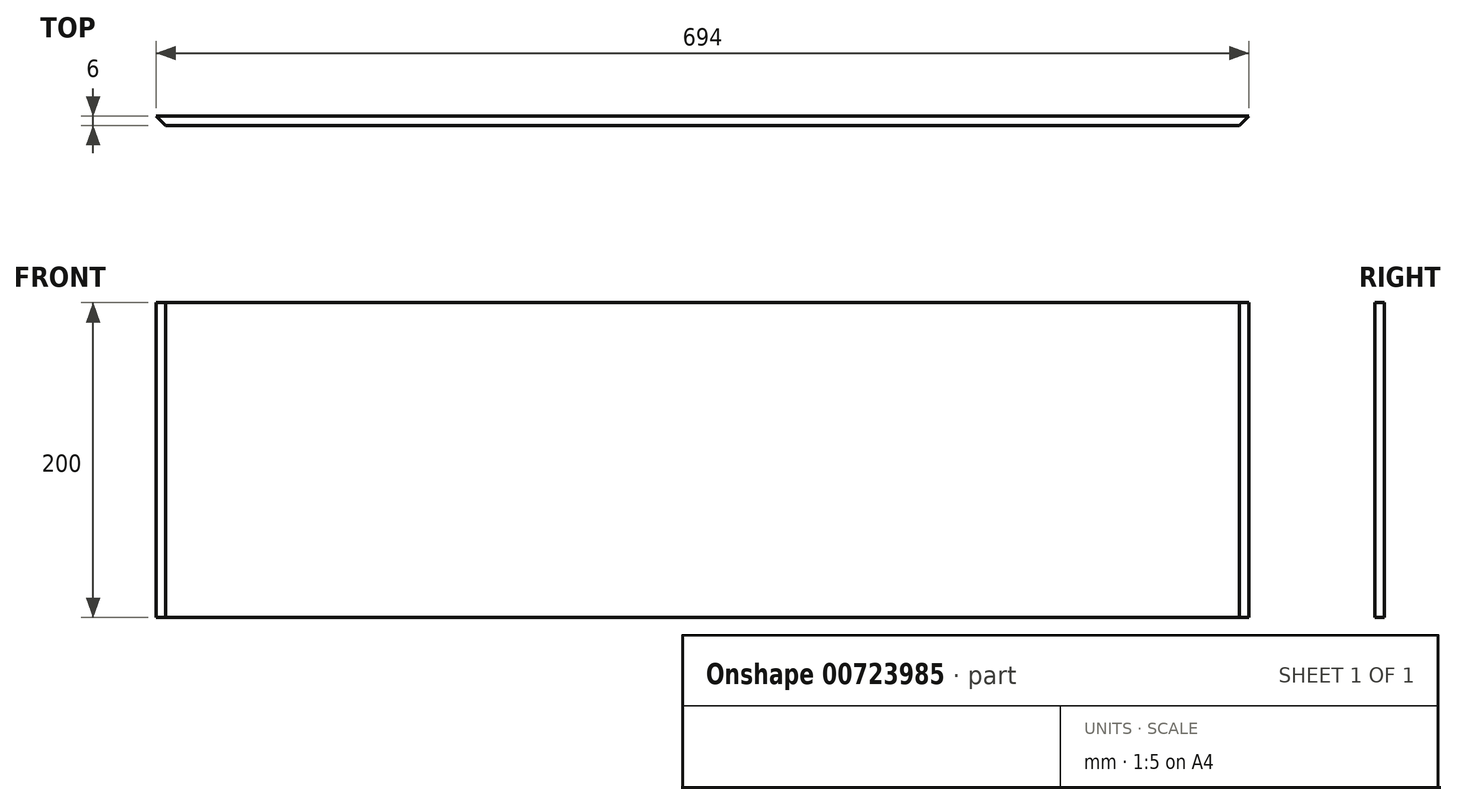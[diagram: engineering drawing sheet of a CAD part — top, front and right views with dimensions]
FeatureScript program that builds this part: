
annotation { "Feature Type Name" : "Feature", "Feature Type Description" : "" }
export const myFeature = defineFeature(function(context is Context, id is Id, definition is map)
    precondition{}
    {
        {
            var Q0;
            Q0=qCreatedBy(makeId("Front.planeOp"),FACE);
            var sketch = newSketch(context, id + "F0", { "sketchPlane" : qUnion([Q0])});
            skLineSegment(sketch, "E0.bottom", {"start": v(-347, 100) * mm, "end": v(347, 100) * mm});
            skLineSegment(sketch, "E0.top", {"start": v(-347, -100) * mm, "end": v(347, -100) * mm});
            skLineSegment(sketch, "E0.left", {"start": v(-347, 100) * mm, "end": v(-347, -100) * mm});
            skLineSegment(sketch, "E0.right", {"start": v(347, 100) * mm, "end": v(347, -100) * mm});
            skLineSegment(sketch, "E1", {"start": v(-347, 100) * mm, "end": v(347, -100) * mm, "construction": true});
            skLineSegment(sketch, "E2", {"start": v(347, 100) * mm, "end": v(-347, -100) * mm, "construction": true});
            skSolve(sketch);
        }
        {
            var Q0;
            Q0=qSketchRegion(id+"F0",true);
            extrude(context, id + "F1", {"entities" : qUnion([Q0]), "depth" : 6 * mm, "offsetDistance" : 25 * mm});
        }
        {
            var Q0;
            Q0=makeQuery(id+"F1.opExtrude","CAP_EDGE",EDGE,{"disambiguationData":[OSD([sQuery(id+"F0.wireOp",EDGE,"E0.right")])],"isStart":false});
            var Q1;
            Q1=makeQuery(id+"F1.opExtrude","CAP_EDGE",EDGE,{"disambiguationData":[OSD([sQuery(id+"F0.wireOp",EDGE,"E0.left")])],"isStart":false});
            chamfer(context, id + "F2", {"entities" : qUnion([Q0, Q1]), "width" : 6 * mm, "tangentPropagation" : true});
        }
    });
